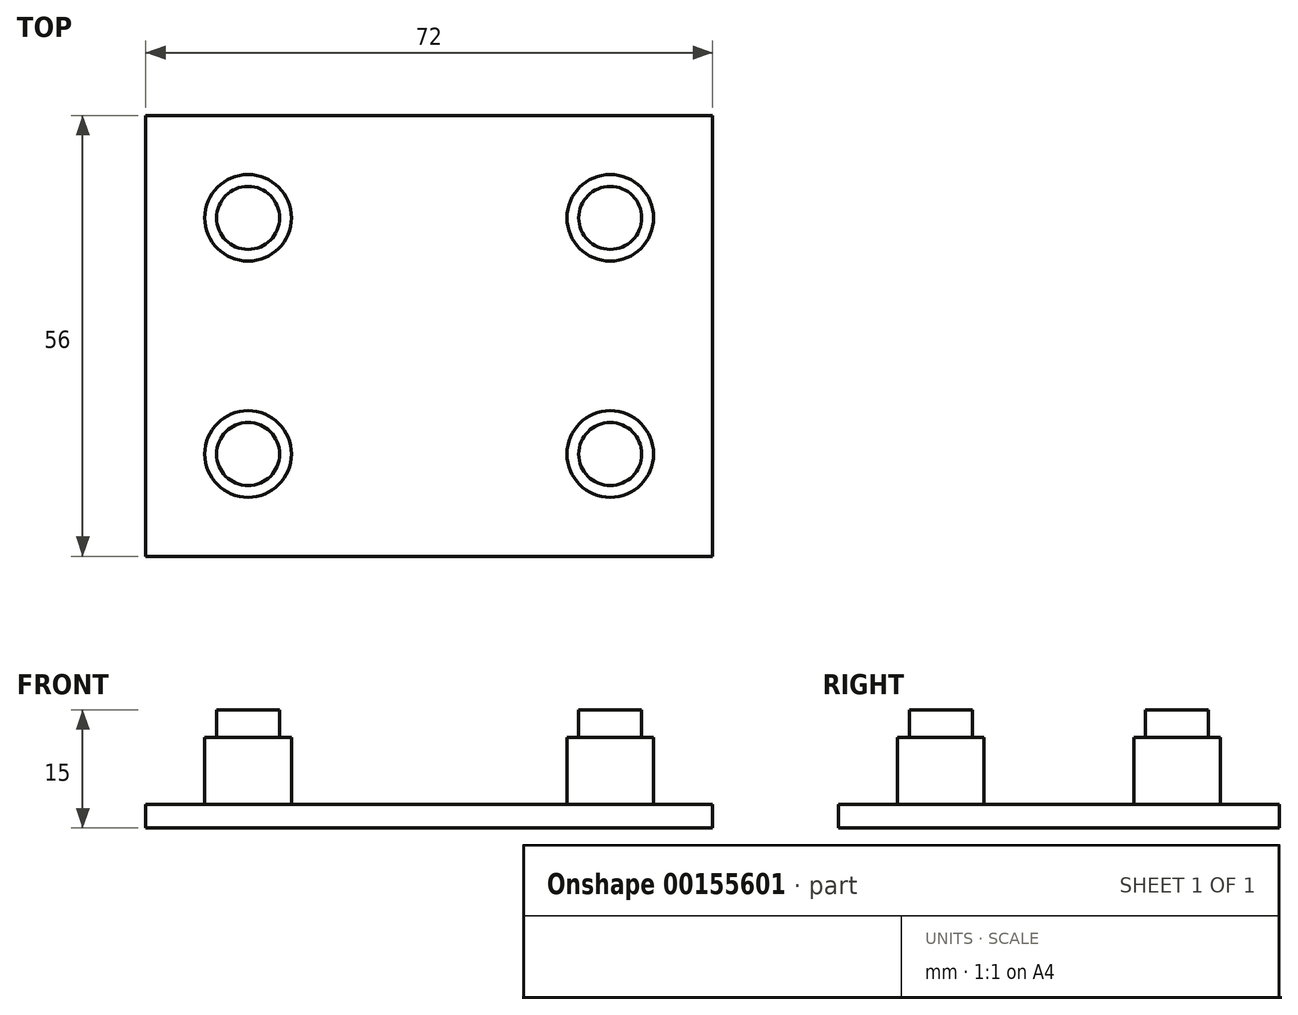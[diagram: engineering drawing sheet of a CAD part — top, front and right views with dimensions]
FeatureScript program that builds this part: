
annotation { "Feature Type Name" : "Feature", "Feature Type Description" : "" }
export const myFeature = defineFeature(function(context is Context, id is Id, definition is map)
    precondition{}
    {
        {
            var Q0;
            Q0=qCreatedBy(makeId("Top.planeOp"),FACE);
            var sketch = newSketch(context, id + "F0", { "sketchPlane" : qUnion([Q0])});
            skLineSegment(sketch, "E0.bottom", {"start": v(0, 0) * mm, "end": v(72, 0) * mm});
            skLineSegment(sketch, "E0.top", {"start": v(0, 56) * mm, "end": v(72, 56) * mm});
            skLineSegment(sketch, "E0.left", {"start": v(0, 0) * mm, "end": v(0, 56) * mm});
            skLineSegment(sketch, "E0.right", {"start": v(72, 0) * mm, "end": v(72, 56) * mm});
            skLineSegment(sketch, "E1", {"start": v(26, 0) * mm, "end": v(26, 56) * mm, "construction": true});
            skLineSegment(sketch, "E2", {"start": v(46, 56) * mm, "end": v(46, 0) * mm, "construction": true});
            skCircle(sketch, "E3", {"center": v(13, 13) * mm, "radius": 11 * mm, "construction": true});
            skCircle(sketch, "E4", {"center": v(13, 13) * mm, "radius": 4 * mm});
            skCircle(sketch, "E5", {"center": v(13, 13) * mm, "radius": 5.5 * mm});
            skCircle(sketch, "E6.0.1.0", {"center": v(13, 43) * mm, "radius": 11 * mm, "construction": true});
            skCircle(sketch, "E6.0.1.1", {"center": v(13, 43) * mm, "radius": 5.5 * mm});
            skCircle(sketch, "E6.0.1.2", {"center": v(13, 43) * mm, "radius": 4 * mm});
            skCircle(sketch, "E6.1.0.0", {"center": v(59, 13) * mm, "radius": 11 * mm, "construction": true});
            skCircle(sketch, "E6.1.0.1", {"center": v(59, 13) * mm, "radius": 5.5 * mm});
            skCircle(sketch, "E6.1.0.2", {"center": v(59, 13) * mm, "radius": 4 * mm});
            skCircle(sketch, "E6.1.1.0", {"center": v(59, 43) * mm, "radius": 11 * mm, "construction": true});
            skCircle(sketch, "E6.1.1.1", {"center": v(59, 43) * mm, "radius": 5.5 * mm});
            skCircle(sketch, "E6.1.1.2", {"center": v(59, 43) * mm, "radius": 4 * mm});
            skLineSegment(sketch, "E6.direction1", {"start": v(13, 13) * mm, "end": v(59, 13) * mm, "construction": true});
            skLineSegment(sketch, "E6.direction2", {"start": v(13, 13) * mm, "end": v(13, 43) * mm, "construction": true});
            skSolve(sketch);
        }
        {
            var Q0;
            Q0 = qSketchRegion(id + "F0", true);
            extrude(context, id + "F1", {"entities" : qUnion([Q0]), "depth" : 3 * mm});
        }
        {
            var Q0;
            Q0=makeQuery(id+"F0.imprint","IMPRINT",FACE,{"disambiguationData":[TD([[makeQuery(id+"F0.imprint","IMPRINT",EDGE,{"derivedFrom":sQuery(id+"F0.wireOp",EDGE,"E6.1.0.1")}),1.0]])]});
            var Q1;
            Q1=makeQuery(id+"F0.imprint","IMPRINT",FACE,{"disambiguationData":[TD([[makeQuery(id+"F0.imprint","IMPRINT",EDGE,{"derivedFrom":sQuery(id+"F0.wireOp",EDGE,"E6.1.1.1")}),1.0]])]});
            var Q2;
            Q2=makeQuery(id+"F0.imprint","IMPRINT",FACE,{"disambiguationData":[TD([[makeQuery(id+"F0.imprint","IMPRINT",EDGE,{"derivedFrom":sQuery(id+"F0.wireOp",EDGE,"E6.0.1.1")}),1.0]])]});
            var Q3;
            Q3=makeQuery(id+"F0.imprint","IMPRINT",FACE,{"disambiguationData":[TD([[makeQuery(id+"F0.imprint","IMPRINT",EDGE,{"derivedFrom":sQuery(id+"F0.wireOp",EDGE,"E4")}),-1.0]])]});
            extrude(context, id + "F2", {"entities" : qUnion([Q0, Q1, Q2, Q3]), "operationType" : NewBodyOperationType.ADD, "depth" : (3 + 20 / 2 - 7 / 2 + 2) * mm});
        }
        {
            var Q0;
            Q0=makeQuery(id+"F0.imprint","IMPRINT",FACE,{"disambiguationData":[TD([[makeQuery(id+"F0.imprint","IMPRINT",EDGE,{"derivedFrom":sQuery(id+"F0.wireOp",EDGE,"E6.0.1.2")}),1.0]])]});
            var Q1;
            Q1=makeQuery(id+"F0.imprint","IMPRINT",FACE,{"disambiguationData":[TD([[makeQuery(id+"F0.imprint","IMPRINT",EDGE,{"derivedFrom":sQuery(id+"F0.wireOp",EDGE,"E6.1.1.2")}),1.0]])]});
            var Q2;
            Q2=makeQuery(id+"F0.imprint","IMPRINT",FACE,{"disambiguationData":[TD([[makeQuery(id+"F0.imprint","IMPRINT",EDGE,{"derivedFrom":sQuery(id+"F0.wireOp",EDGE,"E6.1.0.2")}),1.0]])]});
            var Q3;
            Q3=makeQuery(id+"F0.imprint","IMPRINT",FACE,{"disambiguationData":[TD([[makeQuery(id+"F0.imprint","IMPRINT",EDGE,{"derivedFrom":sQuery(id+"F0.wireOp",EDGE,"E4")}),1.0]])]});
            extrude(context, id + "F3", {"entities" : qUnion([Q0, Q1, Q2, Q3]), "operationType" : NewBodyOperationType.ADD, "depth" : (3 + 20 / 2 + 2) * mm});
        }
    });
